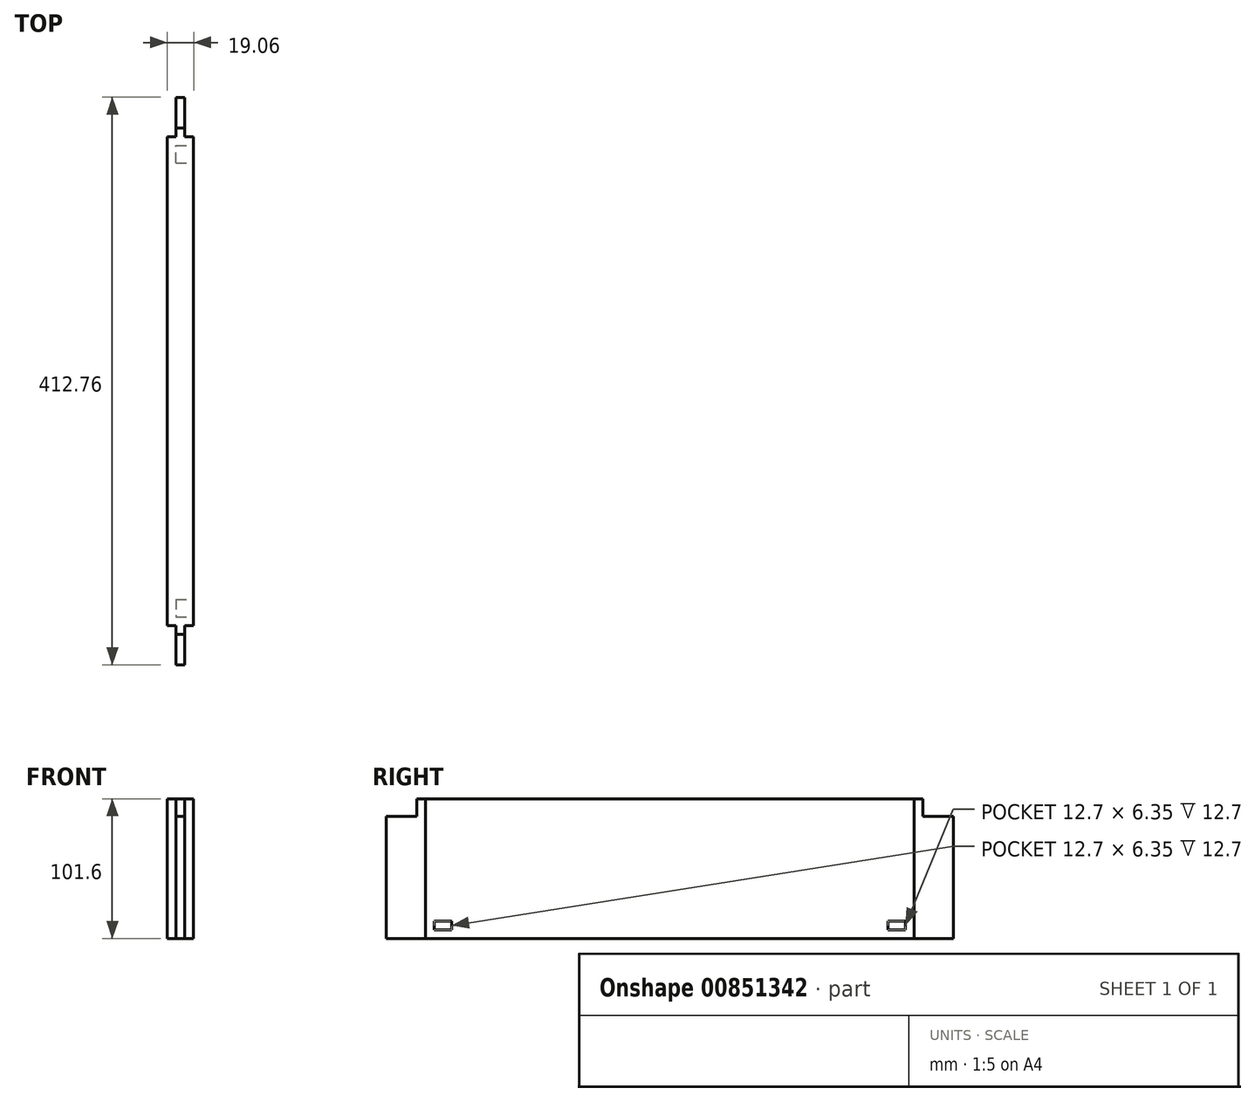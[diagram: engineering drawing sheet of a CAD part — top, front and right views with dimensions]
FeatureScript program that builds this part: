
annotation { "Feature Type Name" : "Feature", "Feature Type Description" : "" }
export const myFeature = defineFeature(function(context is Context, id is Id, definition is map)
    precondition{}
    {
        {
            var Q0;
            Q0=qCreatedBy(makeId("Right.planeOp"),FACE);
            var sketch = newSketch(context, id + "F0", { "sketchPlane" : qUnion([Q0])});
            skLineSegment(sketch, "E0.bottom", {"start": v(-177.8, 0) * mm, "end": v(177.8, 0) * mm});
            skLineSegment(sketch, "E0.top", {"start": v(-177.8, -101.6) * mm, "end": v(177.8, -101.6) * mm});
            skLineSegment(sketch, "E0.left", {"start": v(-177.8, 0) * mm, "end": v(-177.8, -101.6) * mm});
            skLineSegment(sketch, "E0.right", {"start": v(177.8, 0) * mm, "end": v(177.8, -101.6) * mm});
            skLineSegment(sketch, "E1", {"start": v(-177.8, 0) * mm, "end": v(-184.15, 0) * mm});
            skLineSegment(sketch, "E2", {"start": v(-184.15, 0) * mm, "end": v(-184.15, -12.7) * mm});
            skLineSegment(sketch, "E3", {"start": v(-184.15, -12.7) * mm, "end": v(-206.38, -12.7) * mm});
            skLineSegment(sketch, "E4", {"start": v(-206.38, -12.7) * mm, "end": v(-206.38, -101.6) * mm});
            skLineSegment(sketch, "E5", {"start": v(-206.38, -101.6) * mm, "end": v(-177.8, -101.6) * mm});
            skLineSegment(sketch, "E6.MirrorCS", {"start": v(177.8, 0) * mm, "end": v(184.15, 0) * mm});
            skLineSegment(sketch, "E7.MirrorCS", {"start": v(206.38, -101.6) * mm, "end": v(177.8, -101.6) * mm});
            skLineSegment(sketch, "E8.MirrorCS", {"start": v(184.15, 0) * mm, "end": v(184.15, -12.7) * mm});
            skLineSegment(sketch, "E9.MirrorCS", {"start": v(184.15, -12.7) * mm, "end": v(206.38, -12.7) * mm});
            skLineSegment(sketch, "E10.MirrorCS", {"start": v(206.38, -12.7) * mm, "end": v(206.38, -101.6) * mm});
            skSolve(sketch);
        }
        {
            var Q0;
            Q0=makeQuery(id+"F0.imprint","IMPRINT",FACE,{"disambiguationData":[TD([[makeQuery(id+"F0.imprint","IMPRINT",EDGE,{"derivedFrom":sQuery(id+"F0.wireOp",EDGE,"E0.bottom")}),-1.0]])]});
            var Q1;
            Q1=makeQuery(id+"F0.imprint","IMPRINT",FACE,{"disambiguationData":[TD([[makeQuery(id+"F0.imprint","IMPRINT",EDGE,{"derivedFrom":sQuery(id+"F0.wireOp",EDGE,"k3Rr6xLO-2B4O-ynhO-6V3V-HA5jG63kI4td.bottom")}),1.0]])]});
            var Q2;
            Q2=makeQuery(id+"F0.imprint","IMPRINT",FACE,{"disambiguationData":[TD([[makeQuery(id+"F0.imprint","IMPRINT",EDGE,{"derivedFrom":sQuery(id+"F0.wireOp",EDGE,"75d1bac3-520c-4986-a10e-221c74be0fa60.MirrorCS")}),-1.0]])]});
            extrude(context, id + "F1", {"entities" : qUnion([Q0, Q1, Q2]), "depth" : 19.05 * mm, "offsetDistance" : 25.4 * mm, "symmetric" : true});
        }
        {
            var Q0;
            Q0=makeQuery(id+"F0.imprint","IMPRINT",FACE,{"disambiguationData":[TD([[makeQuery(id+"F0.imprint","IMPRINT",EDGE,{"derivedFrom":sQuery(id+"F0.wireOp",EDGE,"E0.left")}),-1.0]])]});
            var Q1;
            Q1=makeQuery(id+"F0.imprint","IMPRINT",FACE,{"disambiguationData":[TD([[makeQuery(id+"F0.imprint","IMPRINT",EDGE,{"derivedFrom":sQuery(id+"F0.wireOp",EDGE,"E0.right")}),1.0]])]});
            extrude(context, id + "F2", {"entities" : qUnion([Q0, Q1]), "operationType" : NewBodyOperationType.ADD, "depth" : 6.35 * mm, "offsetDistance" : 25.4 * mm, "symmetric" : true});
        }
        {
            var Q0;
            Q0=makeQuery(id+"F1.opExtrude","CAP_FACE",FACE,{"disambiguationData":[OSD([sQuery(id+"F0.wireOp",EDGE,"E0.bottom"),sQuery(id+"F0.wireOp",EDGE,"E0.top"),sQuery(id+"F0.wireOp",EDGE,"E0.left"),sQuery(id+"F0.wireOp",EDGE,"E0.right")])],"isStart":false});
            var sketch = newSketch(context, id + "F3", { "sketchPlane" : qUnion([Q0])});
            skLineSegment(sketch, "E11.bottom", {"start": v(-177.8, -101.6) * mm, "end": v(-158.75, -101.6) * mm, "construction": true});
            skLineSegment(sketch, "E11.top", {"start": v(-177.8, -88.9) * mm, "end": v(-158.75, -88.9) * mm, "construction": true});
            skLineSegment(sketch, "E11.left", {"start": v(-177.8, -101.6) * mm, "end": v(-177.8, -88.9) * mm, "construction": true});
            skLineSegment(sketch, "E11.right", {"start": v(-158.75, -101.6) * mm, "end": v(-158.75, -88.9) * mm, "construction": true});
            skLineSegment(sketch, "E12.bottom", {"start": v(-158.75, -88.9) * mm, "end": v(-171.45, -88.9) * mm});
            skLineSegment(sketch, "E12.top", {"start": v(-158.75, -95.25) * mm, "end": v(-171.45, -95.25) * mm});
            skLineSegment(sketch, "E12.left", {"start": v(-158.75, -88.9) * mm, "end": v(-158.75, -95.25) * mm});
            skLineSegment(sketch, "E12.right", {"start": v(-171.45, -88.9) * mm, "end": v(-171.45, -95.25) * mm});
            skLineSegment(sketch, "E13.MirrorCS", {"start": v(171.45, -88.9) * mm, "end": v(171.45, -95.25) * mm});
            skLineSegment(sketch, "E14.MirrorCS", {"start": v(158.75, -95.25) * mm, "end": v(171.45, -95.25) * mm});
            skLineSegment(sketch, "E15.MirrorCS", {"start": v(158.75, -88.9) * mm, "end": v(158.75, -95.25) * mm});
            skLineSegment(sketch, "E16.MirrorCS", {"start": v(158.75, -88.9) * mm, "end": v(171.45, -88.9) * mm});
            skSolve(sketch);
        }
        {
            var Q0;
            Q0 = qSketchRegion(id + "F3", true);
            extrude(context, id + "F4", {"entities" : qUnion([Q0]), "operationType" : NewBodyOperationType.REMOVE, "oppositeDirection" : true, "depth" : 12.7 * mm, "offsetDistance" : 25.4 * mm});
        }
    });
